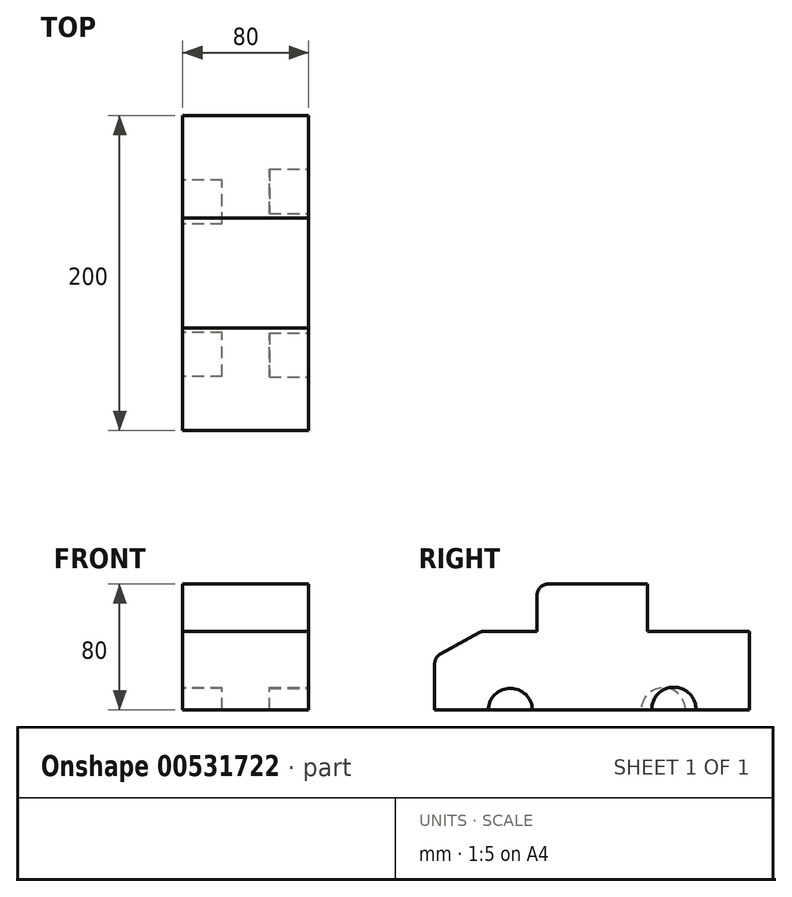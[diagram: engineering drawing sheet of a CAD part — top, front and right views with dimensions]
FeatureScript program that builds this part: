
annotation { "Feature Type Name" : "Feature", "Feature Type Description" : "" }
export const myFeature = defineFeature(function(context is Context, id is Id, definition is map)
    precondition{}
    {
        {
            var Q0;
            Q0=qCreatedBy(makeId("Right.planeOp"),FACE);
            var sketch = newSketch(context, id + "F0", { "sketchPlane" : qUnion([Q0])});
            skLineSegment(sketch, "E0", {"start": v(-73.54, -41.31) * mm, "end": v(126.46, -41.31) * mm});
            skLineSegment(sketch, "E1", {"start": v(126.46, -41.31) * mm, "end": v(126.46, 8.69) * mm});
            skLineSegment(sketch, "E2", {"start": v(126.46, 8.69) * mm, "end": v(61.46, 8.69) * mm});
            skLineSegment(sketch, "E3", {"start": v(61.46, 8.69) * mm, "end": v(61.46, 38.69) * mm});
            skLineSegment(sketch, "E4", {"start": v(61.46, 38.69) * mm, "end": v(-8.54, 38.69) * mm});
            skLineSegment(sketch, "E5", {"start": v(-8.54, 38.69) * mm, "end": v(-8.54, 8.69) * mm});
            skLineSegment(sketch, "E6", {"start": v(-8.54, 8.69) * mm, "end": v(-43.54, 8.69) * mm});
            skLineSegment(sketch, "E7", {"start": v(-43.54, 8.69) * mm, "end": v(-73.54, -7.89) * mm});
            skLineSegment(sketch, "E8", {"start": v(-73.54, -7.89) * mm, "end": v(-73.54, -41.31) * mm});
            skSolve(sketch);
        }
        {
            var Q0;
            Q0=makeQuery(id+"F0.imprint","IMPRINT",FACE,{"disambiguationData":[TD([[makeQuery(id+"F0.imprint","IMPRINT",EDGE,{"derivedFrom":sQuery(id+"F0.wireOp",EDGE,"E0")}),1.0]])]});
            extrude(context, id + "F1", {"entities" : qUnion([Q0]), "depth" : 80 * mm, "offsetDistance" : 25 * mm});
        }
        {
            var Q0;
            Q0=makeQuery(id+"F1.opExtrude","CAP_FACE",FACE,{"disambiguationData":[OSD([sQuery(id+"F0.wireOp",EDGE,"E0"),sQuery(id+"F0.wireOp",EDGE,"E1"),sQuery(id+"F0.wireOp",EDGE,"E2"),sQuery(id+"F0.wireOp",EDGE,"E3"),sQuery(id+"F0.wireOp",EDGE,"E4"),sQuery(id+"F0.wireOp",EDGE,"E5"),sQuery(id+"F0.wireOp",EDGE,"E6"),sQuery(id+"F0.wireOp",EDGE,"E7"),sQuery(id+"F0.wireOp",EDGE,"E8")])],"isStart":false});
            var sketch = newSketch(context, id + "F2", { "sketchPlane" : qUnion([Q0])});
            skArc(sketch, "E9", {"start": v(-11.52, -41.31) * mm, "mid": v(-25.52, -27.57) * mm, "end": v(-39.51, -41.31) * mm});
            skSolve(sketch);
        }
        {
            var Q0;
            Q0=makeQuery(id+"F1.opExtrude","CAP_FACE",FACE,{"disambiguationData":[OSD([sQuery(id+"F0.wireOp",EDGE,"E0"),sQuery(id+"F0.wireOp",EDGE,"E1"),sQuery(id+"F0.wireOp",EDGE,"E2"),sQuery(id+"F0.wireOp",EDGE,"E3"),sQuery(id+"F0.wireOp",EDGE,"E4"),sQuery(id+"F0.wireOp",EDGE,"E5"),sQuery(id+"F0.wireOp",EDGE,"E6"),sQuery(id+"F0.wireOp",EDGE,"E7"),sQuery(id+"F0.wireOp",EDGE,"E8")])],"isStart":true});
            var sketch = newSketch(context, id + "F3", { "sketchPlane" : qUnion([Q0])});
            skArc(sketch, "E10", {"start": v(39.16, -41.31) * mm, "mid": v(25.16, -27.67) * mm, "end": v(11.17, -41.31) * mm});
            skArc(sketch, "E11", {"start": v(-56.89, -41.31) * mm, "mid": v(-70.86, -28.21) * mm, "end": v(-84.83, -41.31) * mm});
            skSolve(sketch);
        }
        {
            var Q0;
            {var subQ0=sQuery(id+"F3.wireOp",EDGE,"E10");Q0=makeQuery(id+"F3.imprint","IMPRINT",FACE,{"disambiguationData":[TD([[makeQuery(id+"F3.imprint","IMPRINT",EDGE,{"derivedFrom":subQ0}),1.0]])]});}
            extrude(context, id + "F4", {"entities" : qUnion([Q0]), "operationType" : NewBodyOperationType.REMOVE, "oppositeDirection" : true, "depth" : 25 * mm, "offsetDistance" : 25 * mm});
        }
        {
            var Q0;
            Q0=makeQuery(id+"F1.opExtrude","CAP_FACE",FACE,{"disambiguationData":[OSD([sQuery(id+"F0.wireOp",EDGE,"E0"),sQuery(id+"F0.wireOp",EDGE,"E1"),sQuery(id+"F0.wireOp",EDGE,"E2"),sQuery(id+"F0.wireOp",EDGE,"E3"),sQuery(id+"F0.wireOp",EDGE,"E4"),sQuery(id+"F0.wireOp",EDGE,"E5"),sQuery(id+"F0.wireOp",EDGE,"E6"),sQuery(id+"F0.wireOp",EDGE,"E7"),sQuery(id+"F0.wireOp",EDGE,"E8")])],"isStart":true});
            var sketch = newSketch(context, id + "F5", { "sketchPlane" : qUnion([Q0])});
            skArc(sketch, "E12", {"start": v(-57.65, -41.31) * mm, "mid": v(-71.65, -27.31) * mm, "end": v(-85.65, -41.31) * mm});
            skSolve(sketch);
        }
        {
            var Q0;
            {var subQ0=sQuery(id+"F5.wireOp",EDGE,"E12");Q0=makeQuery(id+"F5.imprint","IMPRINT",FACE,{"disambiguationData":[TD([[makeQuery(id+"F5.imprint","IMPRINT",EDGE,{"derivedFrom":subQ0}),1.0]])]});}
            extrude(context, id + "F6", {"entities" : qUnion([Q0]), "operationType" : NewBodyOperationType.REMOVE, "oppositeDirection" : true, "depth" : 25 * mm, "offsetDistance" : 25 * mm});
        }
        {
            var Q0;
            {var subQ0=sQuery(id+"F2.wireOp",EDGE,"E9");Q0=makeQuery(id+"F2.imprint","IMPRINT",FACE,{"disambiguationData":[TD([[makeQuery(id+"F2.imprint","IMPRINT",EDGE,{"derivedFrom":subQ0}),1.0]])]});}
            extrude(context, id + "F7", {"entities" : qUnion([Q0]), "operationType" : NewBodyOperationType.REMOVE, "oppositeDirection" : true, "depth" : 25 * mm, "offsetDistance" : 25 * mm});
        }
        {
            var Q0;
            Q0=makeQuery(id+"F1.opExtrude","CAP_FACE",FACE,{"disambiguationData":[OSD([sQuery(id+"F0.wireOp",EDGE,"E0"),sQuery(id+"F0.wireOp",EDGE,"E1"),sQuery(id+"F0.wireOp",EDGE,"E2"),sQuery(id+"F0.wireOp",EDGE,"E3"),sQuery(id+"F0.wireOp",EDGE,"E4"),sQuery(id+"F0.wireOp",EDGE,"E5"),sQuery(id+"F0.wireOp",EDGE,"E6"),sQuery(id+"F0.wireOp",EDGE,"E7"),sQuery(id+"F0.wireOp",EDGE,"E8")])],"isStart":false});
            var sketch = newSketch(context, id + "F8", { "sketchPlane" : qUnion([Q0])});
            skArc(sketch, "E13", {"start": v(92.35, -41.31) * mm, "mid": v(78.36, -26.88) * mm, "end": v(64.36, -41.31) * mm});
            skSolve(sketch);
        }
        {
            var Q0;
            {var subQ0=sQuery(id+"F8.wireOp",EDGE,"E13");Q0=makeQuery(id+"F8.imprint","IMPRINT",FACE,{"disambiguationData":[TD([[makeQuery(id+"F8.imprint","IMPRINT",EDGE,{"derivedFrom":subQ0}),1.0]])]});}
            extrude(context, id + "F9", {"entities" : qUnion([Q0]), "operationType" : NewBodyOperationType.REMOVE, "oppositeDirection" : true, "depth" : 25 * mm, "offsetDistance" : 25 * mm});
        }
        {
            var Q0;
            Q0=makeQuery(id+"F1.opExtrude","SWEPT_EDGE",EDGE,{"disambiguationData":[OSD([sQuery(id+"F0.wireOp",EDGE,"E4"),sQuery(id+"F0.wireOp",EDGE,"E5")])]});
            var Q1;
            Q1=makeQuery(id+"F1.opExtrude","SWEPT_EDGE",EDGE,{"disambiguationData":[OSD([sQuery(id+"F0.wireOp",EDGE,"E7"),sQuery(id+"F0.wireOp",EDGE,"E8")])]});
            var Q2;
            Q2=makeQuery(id+"F1.opExtrude","SWEPT_EDGE",EDGE,{"disambiguationData":[OSD([sQuery(id+"F0.wireOp",EDGE,"E6"),sQuery(id+"F0.wireOp",EDGE,"E7")])]});
            fillet(context, id + "F10", {"entities" : qUnion([Q0, Q1, Q2]), "radius" : 7 * mm, "tangentPropagation" : true, "allowEdgeOverflow" : false});
        }
    });
